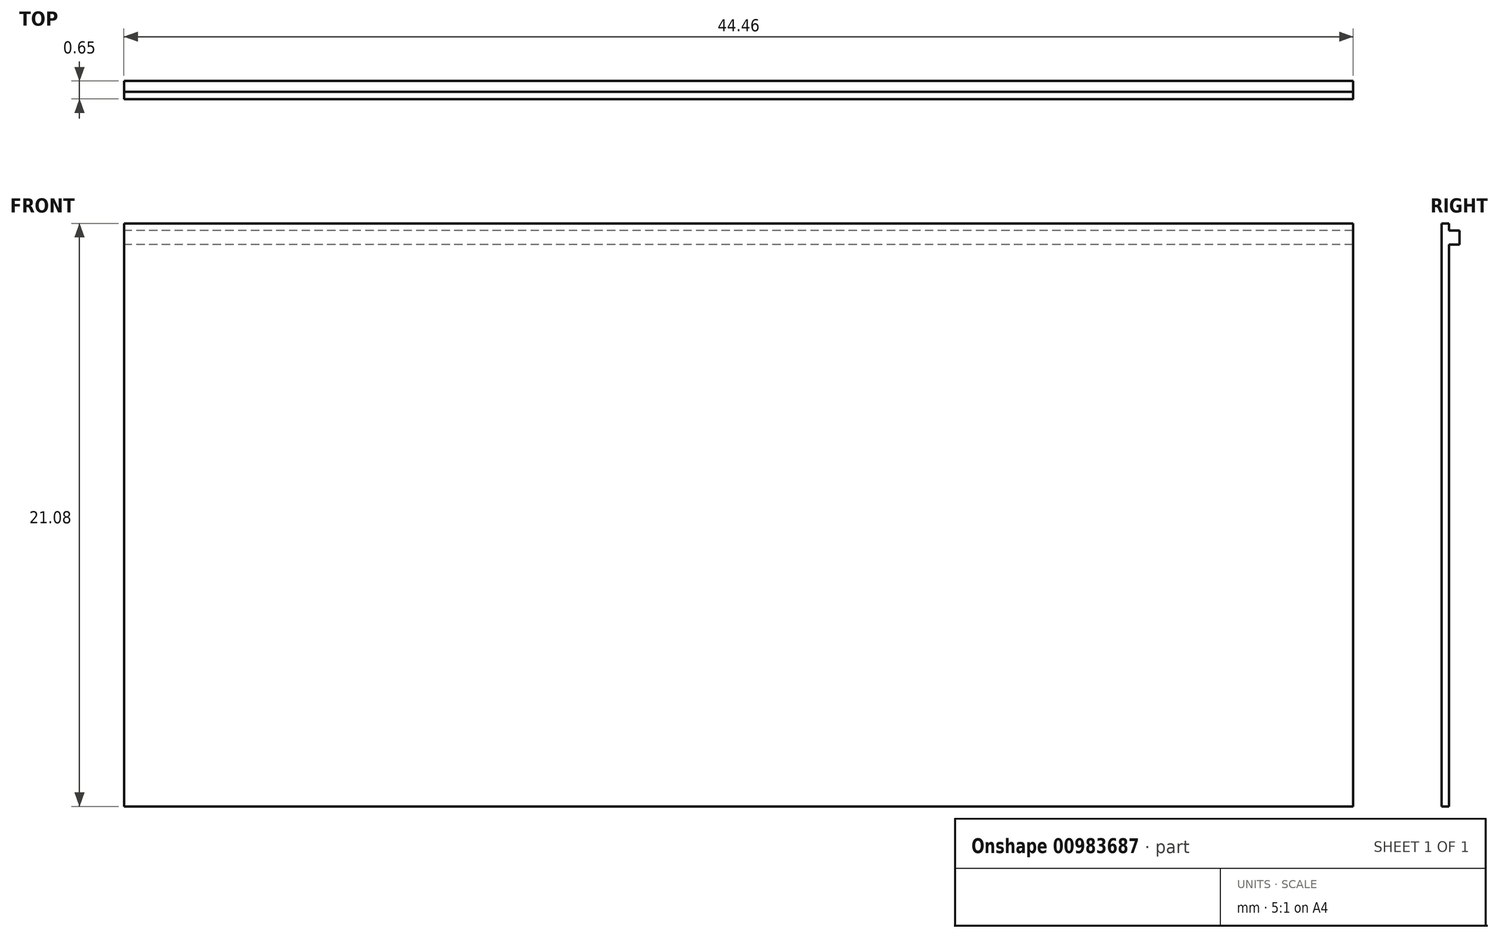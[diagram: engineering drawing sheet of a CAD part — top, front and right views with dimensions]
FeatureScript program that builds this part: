
annotation { "Feature Type Name" : "Feature", "Feature Type Description" : "" }
export const myFeature = defineFeature(function(context is Context, id is Id, definition is map)
    precondition{}
    {
        {
            var Q0;
            Q0=qCreatedBy(makeId("Front.planeOp"),FACE);
            var sketch = newSketch(context, id + "F0", { "sketchPlane" : qUnion([Q0])});
            skLineSegment(sketch, "E0.bottom", {"start": v(22.23, 10.54) * mm, "end": v(-22.23, 10.54) * mm});
            skLineSegment(sketch, "E0.top", {"start": v(22.23, -10.54) * mm, "end": v(-22.23, -10.54) * mm});
            skLineSegment(sketch, "E0.left", {"start": v(22.22, 10.54) * mm, "end": v(22.23, -10.54) * mm});
            skLineSegment(sketch, "E0.right", {"start": v(-22.23, 10.54) * mm, "end": v(-22.23, -10.54) * mm});
            skPoint(sketch, "E0.middle", {"position": v(0, 0) * mm});
            skSolve(sketch);
        }
        {
            var Q0;
            Q0 = qSketchRegion(id + "F0", true);
            extrude(context, id + "F1", {"entities" : qUnion([Q0]), "depth" : 0.26 * mm, "offsetDistance" : 25.4 * mm});
        }
        {
            var Q0;
            Q0=qCreatedBy(makeId("Right.planeOp"),FACE);
            var sketch = newSketch(context, id + "F2", { "sketchPlane" : qUnion([Q0])});
            skLineSegment(sketch, "E1.bottom", {"start": v(-3.2, -0.98) * mm, "end": v(-3.2, -0.98) * mm});
            skLineSegment(sketch, "E2.bottom", {"start": v(0, 10.54) * mm, "end": v(0, 10.54) * mm});
            skLineSegment(sketch, "E2.top", {"start": v(0, -10.54) * mm, "end": v(0, -10.54) * mm});
            skLineSegment(sketch, "E2.left", {"start": v(0, 10.29) * mm, "end": v(0, -10.54) * mm});
            skLineSegment(sketch, "E2.right", {"start": v(0, 10.29) * mm, "end": v(0, 9.78) * mm});
            skPoint(sketch, "E2.middle", {"position": v(0, 0) * mm});
            skLineSegment(sketch, "E3", {"start": v(0, 10.29) * mm, "end": v(0.4, 10.29) * mm});
            skLineSegment(sketch, "E4", {"start": v(0.4, 10.29) * mm, "end": v(0.4, 9.78) * mm});
            skLineSegment(sketch, "E5", {"start": v(0.4, 9.78) * mm, "end": v(0, 9.78) * mm});
            skLineSegment(sketch, "E6", {"start": v(0, 9.78) * mm, "end": v(0, 10.29) * mm});
            skLineSegment(sketch, "E7.trimOffspring", {"start": v(0, 0) * mm, "end": v(0, -10.54) * mm});
            skSolve(sketch);
        }
        {
            var Q0;
            Q0 = qSketchRegion(id + "F2", true);
            extrude(context, id + "F3", {"entities" : qUnion([Q0]), "operationType" : NewBodyOperationType.ADD, "endBound" : BoundingType.SYMMETRIC, "depth" : 44.45 * mm, "offsetDistance" : 25.4 * mm});
        }
    });
